# Revit family: 303_R25X_
name_source: partatom
category: Pipe Accessories
revit_build: Autodesk Revit 2018 (Build: 20170223_1515(x64)
units: mm (PartAtom-declared; Revit-internal decimal feet)

## family parameters
Always vertical = Yes
Cut with Voids When Loaded = No
Part Type = Valve - Breaks Into
Round Connector Dimension = Use Diameter
Shared = No
Work Plane-Based = No

## types (5) — shared parameters
CAT0 = Yes
CAT1 = No
Description = Manual angle valve, screwed ends
J3 = 8 mm  [stored 0.0262467 ft]
L2D_Min = 3048 mm
L5 = 3 mm  [stored 0.00984252 ft]
Manufacturer = Giacomini
QmdConnectorList = 301;D;302;D1
SW2 = No
URL = http://www.giacomini.com
Z1 = 5 mm  [stored 0.0164042 ft]
Z2 = 5 mm  [stored 0.0164042 ft]
Z3 = 6 mm  [stored 0.019685 ft]
magiPartTypeId = 303
magiProductFamilyId = R25X*
zero-valued in all types: MC_Default_elevation

## per-type parameters (varying)
- R25X032: B1=8 mm  [stored 0.0262467 ft]; B3=9 mm  [stored 0.0295276 ft]; B4=9 mm  [stored 0.0295276 ft]; CenSd_W2_6=13 mm; D=16 mm; D1=10 mm; G1=8 mm  [stored 0.0262467 ft]; G3=10 mm  [stored 0.0328084 ft]; H3=4 mm  [stored 0.0131234 ft]; H3__ve=-4 mm  [stored -0.0131234 ft]; J5=27 mm  [stored 0.0885827 ft]; L=40 mm  [stored 0.131234 ft]; L2=51 mm; L2D=40 mm  [stored 0.131234 ft]; L3=5 mm  [stored 0.0164042 ft]; L4=5 mm  [stored 0.0164042 ft]; L4__ve=-5 mm  [stored -0.0164042 ft]; L8=8 mm  [stored 0.0262467 ft]; L8__ve=-8 mm  [stored -0.0262467 ft]; M1=21 mm  [stored 0.0688976 ft]; M3=23 mm  [stored 0.0754593 ft]; M3__ve=-23 mm  [stored -0.0754593 ft]; R1=8 mm  [stored 0.0262467 ft]; SW1=Yes; SW3=Yes; SW4=No; W1=12 mm  [stored 0.0393701 ft]; W2=15 mm  [stored 0.0492126 ft]; W2D=16 mm  [stored 0.0524934 ft]; W3=11 mm; X1=23 mm  [stored 0.0754593 ft]; X11=37 mm; X4=6 mm  [stored 0.019685 ft]; Z4=11 mm
- R25X036: B1=11 mm; B3=11 mm; B4=12 mm  [stored 0.0393701 ft]; CenSd_W2_6=16 mm  [stored 0.0524934 ft]; D=22 mm; D1=20 mm; G1=13 mm; G3=15 mm  [stored 0.0492126 ft]; H3=9 mm  [stored 0.0295276 ft]; H3__ve=-9 mm; J5=24 mm  [stored 0.0787402 ft]; L=45 mm; L2=58 mm; L2D=45 mm; L3=6 mm  [stored 0.019685 ft]; L4=6 mm  [stored 0.019685 ft]; L4__ve=-6 mm  [stored -0.019685 ft]; L8=9 mm  [stored 0.0295276 ft]; L8__ve=-9 mm; M1=25 mm  [stored 0.082021 ft]; M3=27 mm  [stored 0.0885827 ft]; M3__ve=-27 mm; R1=13 mm; SW1=No; SW3=No; SW4=Yes; W1=15 mm  [stored 0.0492126 ft]; W2=19 mm  [stored 0.062336 ft]; W2D=22 mm; W3=13 mm; X1=27 mm  [stored 0.0885827 ft]; X11=42 mm  [stored 0.137795 ft]; X4=7 mm  [stored 0.0229659 ft]; Z4=20 mm  [stored 0.0656168 ft]
- R25X035: B1=9 mm  [stored 0.0295276 ft]; B3=10 mm  [stored 0.0328084 ft]; B4=10 mm  [stored 0.0328084 ft]; CenSd_W2_6=16 mm  [stored 0.0524934 ft]; D=18 mm; D1=20 mm; G1=13 mm; G3=15 mm  [stored 0.0492126 ft]; H3=8 mm  [stored 0.0262467 ft]; H3__ve=-8 mm  [stored -0.0262467 ft]; J5=26 mm; L=45 mm; L2=58 mm; L2D=45 mm; L3=6 mm  [stored 0.019685 ft]; L4=6 mm  [stored 0.019685 ft]; L4__ve=-6 mm  [stored -0.019685 ft]; L8=9 mm  [stored 0.0295276 ft]; L8__ve=-9 mm; M1=25 mm  [stored 0.082021 ft]; M3=27 mm  [stored 0.0885827 ft]; M3__ve=-27 mm; R1=13 mm; SW1=No; SW3=No; SW4=Yes; W1=15 mm  [stored 0.0492126 ft]; W2=19 mm  [stored 0.062336 ft]; W2D=18 mm; W3=13 mm; X1=27 mm  [stored 0.0885827 ft]; X11=42 mm  [stored 0.137795 ft]; X4=7 mm  [stored 0.0229659 ft]; Z4=18 mm
- R25X034: B1=9 mm  [stored 0.0295276 ft]; B3=10 mm  [stored 0.0328084 ft]; B4=10 mm  [stored 0.0328084 ft]; CenSd_W2_6=13 mm; D=18 mm; D1=15 mm; G1=10 mm  [stored 0.0328084 ft]; G3=12 mm  [stored 0.0393701 ft]; H3=5 mm  [stored 0.0164042 ft]; H3__ve=-5 mm  [stored -0.0164042 ft]; J5=27 mm  [stored 0.0885827 ft]; L=41 mm; L2=53 mm; L2D=41 mm; L3=6 mm  [stored 0.019685 ft]; L4=6 mm  [stored 0.019685 ft]; L4__ve=-6 mm  [stored -0.019685 ft]; L8=8 mm  [stored 0.0262467 ft]; L8__ve=-8 mm  [stored -0.0262467 ft]; M1=21 mm  [stored 0.0688976 ft]; M3=23 mm  [stored 0.0754593 ft]; M3__ve=-23 mm  [stored -0.0754593 ft]; R1=11 mm; SW1=Yes; SW3=Yes; SW4=No; W1=12 mm  [stored 0.0393701 ft]; W2=15 mm  [stored 0.0492126 ft]; W2D=18 mm; W3=11 mm; X1=23 mm  [stored 0.0754593 ft]; X11=38 mm; X4=6 mm  [stored 0.019685 ft]; Z4=14 mm  [stored 0.0459318 ft]
- R25X033: B1=8 mm  [stored 0.0262467 ft]; B3=9 mm  [stored 0.0295276 ft]; B4=9 mm  [stored 0.0295276 ft]; CenSd_W2_6=13 mm; D=16 mm; D1=15 mm; G1=10 mm  [stored 0.0328084 ft]; G3=12 mm  [stored 0.0393701 ft]; H3=5 mm  [stored 0.0164042 ft]; H3__ve=-5 mm  [stored -0.0164042 ft]; J5=26 mm; L=40 mm  [stored 0.131234 ft]; L2=51 mm; L2D=40 mm  [stored 0.131234 ft]; L3=5 mm  [stored 0.0164042 ft]; L4=5 mm  [stored 0.0164042 ft]; L4__ve=-5 mm  [stored -0.0164042 ft]; L8=8 mm  [stored 0.0262467 ft]; L8__ve=-8 mm  [stored -0.0262467 ft]; M1=21 mm  [stored 0.0688976 ft]; M3=23 mm  [stored 0.0754593 ft]; M3__ve=-23 mm  [stored -0.0754593 ft]; R1=11 mm; SW1=Yes; SW3=Yes; SW4=No; W1=12 mm  [stored 0.0393701 ft]; W2=15 mm  [stored 0.0492126 ft]; W2D=16 mm  [stored 0.0524934 ft]; W3=11 mm; X1=23 mm  [stored 0.0754593 ft]; X11=37 mm; X4=6 mm  [stored 0.019685 ft]; Z4=13 mm

note: column(s) folded — value = type name in every type: magiProductCode, magiProductId

note: [stored X ft] marks values corroborated as IEEE doubles in the binary element streams (Revit-internal decimal feet)

## geometry (parser evidence)
native form markers: Sweep x1
no freeform markers — native parametric forms only
